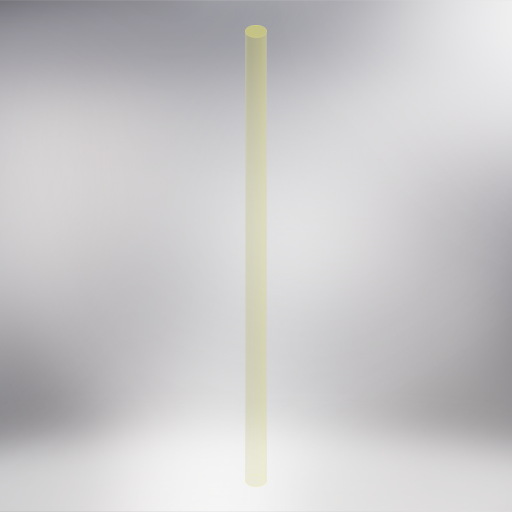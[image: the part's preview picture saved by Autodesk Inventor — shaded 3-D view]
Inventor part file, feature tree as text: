
AUTODESK INVENTOR PART (.ipt)
format: ipt  version: 2024 (Build 280153000, 153)  size: 318,976 bytes
history: native  units: in
note: dims shown in document units (in); Inventor stores cm internally (conversion verified against a paired STEP export)
features: extrude x1, sketch x1
ambient origin geometry x8: Origin, YZ Plane, XZ Plane, XY Plane, X Axis, Y Axis, Z Axis, Center Point
bodies: Solid1 (feature_tree)
feature tree (2):
  extrude  "Extrusion1"  Depth=10.0in TaperAngle=0.0deg
  sketch  "Sketch1"  dims[d0=0.3937in d1=10.0in d2=0.0in]
